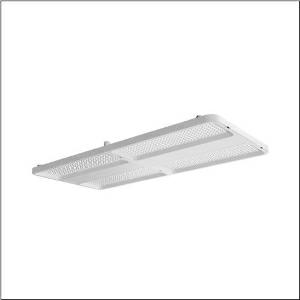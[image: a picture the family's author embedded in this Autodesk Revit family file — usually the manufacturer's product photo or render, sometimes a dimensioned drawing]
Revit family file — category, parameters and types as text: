
# Revit family: highbay_11_maxi_51hn11db5qda
name_source: partatom
category: Lighting Fixtures
units: mm (PartAtom-declared; Revit-internal decimal feet)

## family parameters
Cut with Voids When Loaded = No
Host = Face
Light Source = No
Part Type = Normal
Room Calculation Point = No
Round Connector Dimension = Use Diameter
Shared = No

## types (1)
- --- (1 x LED, 5590 lm, 27.8 W, 5000K)
    Apparent Load = 28 VA
    CIE Flux Codes = 85 97 100 100 100
    Color Rendering = 80
    Color Temperature = 5000K
    Default Elevation = 1800 mm
    Description = high bay luminaire Highbay 11 maxi; direct symmetric narrow distribution, light control with lens of PMMA; UGR ≤ 22 (X = 4H | Y = 8H | S = 0.25H | reflection values 70/50/20); luminous flux: 35.850lm; light colour: 850, colour temperature: 5000K, MacAdam ≤ 2 SDCM (initial), colour rendering: CRI > 80; luminous efficacy: 201,7lm/W; rated service life: 100.000h (L95/B50) at AT= 25°C; control: DALI 2; luminaire connection: terminal, 5-pole, max. 2.5mm² (cable entry for one cable, Ø 8.5..16mm); mains connection: 230..240V, AC/DC 0/50..60Hz; connected load: 177,7W; protection rating (complete): IP66; insulation class (complete): insulation class I (protective earthing); protection symbol: D; impact resistance: IK08; certification: CE, ENEC, VDE, UKCA; luminaire for central battery installations according to DIN EN 60598-2-22, internal wiring halogen-free; luminaire LABS conformity tested according to VDMA 24364:2018-05; corresponds to IFS (International Featured Standards) requirements for safety and quality in the food industry; housing frame of high-performance plastic PA6, matt traffic white (RAL 9016); cover of PMMA; dimension (LxWxH): 946 x 442 x 72mm; permissible operating ambient temperature: -40..+55°C (reducing of maximum allowable ambient temperature of 5°C with ceiling mounting); packaging unit: 1 piece; (delivery without accessories; please order mounting accessories separately)
    Height = 72 mm  [stored 0.23622 ft]
    Lamp = 1 x LED
    Lamp Light Flux = 5590 lm
    Lamp Power = 27.8 W
    Lamp count = 1
    Length = 946 mm
    Luminous efficacy = 201 lm/W
    Manufacturer = Siteco
    ModVariant = No
    Model = 51HN11DB5QDA
    Mounting Place = Ceiling
    Mounting Type = Pendant
    Number of Poles = 1
    OnlyDefault = Yes
    Power Factor = 1
    Product Name = Highbay 11 maxi
    Product group = high bay luminaire
    ProductGroupID = 901
    Protection Class = Protection class I
    Protection Degree = IP 66
    RLX_Detail_Level = 1
    RLX_Emergency_Light_Flux = 0 lm
    RLX_Emergency_Type = 0
    RLX_Emergency_Type_DB = No
    RlxData = <blob elided: 127681 chars, md5=f1363f8a>
    Socket = socket
    Standby Power = 0 W
    System Light Flux = 5590 lm
    System Power = 28 W
    Type Comments = : DC mode (central or group accumulator) initial emergency light level
    Type Image = l_1363244.jpg
    URL = http://relux.com
    VarID = @adj_004529
    Voltage = 0 V
    Weight = 0.00 kg
    Width = 442 mm

note: [stored X ft] marks values corroborated as IEEE doubles in the binary element streams (Revit-internal decimal feet)

## geometry (parser evidence)
native form markers: Blend x4, Sweep x12
no freeform markers — native parametric forms only
